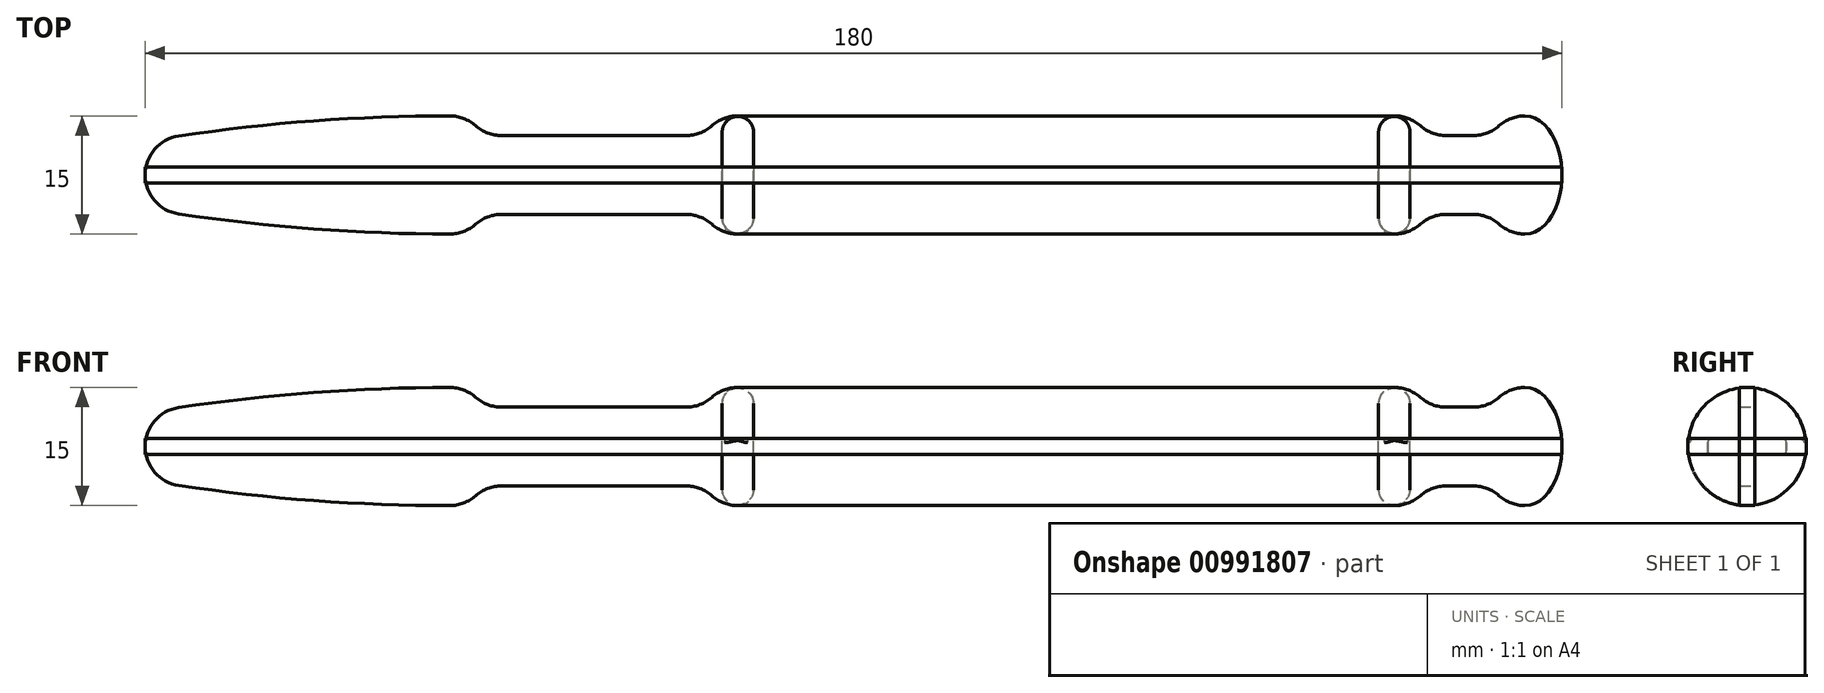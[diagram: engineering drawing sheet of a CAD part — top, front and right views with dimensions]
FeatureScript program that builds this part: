
annotation { "Feature Type Name" : "Feature", "Feature Type Description" : "" }
export const myFeature = defineFeature(function(context is Context, id is Id, definition is map)
    precondition{}
    {
        {
            var Q0;
            Q0=qCreatedBy(makeId("Top.planeOp"),FACE);
            var sketch = newSketch(context, id + "F0", { "sketchPlane" : qUnion([Q0])});
            skLineSegment(sketch, "E0", {"start": v(-90, 0) * mm, "end": v(90, 0) * mm});
            skLineSegment(sketch, "E1.top", {"start": v(-44.7, 5) * mm, "end": v(-21.3, 5) * mm});
            skLineSegment(sketch, "E2.top", {"start": v(75.3, 5) * mm, "end": v(78.7, 5) * mm});
            skLineSegment(sketch, "E3.trimOffspring", {"start": v(-14.7, 7.5) * mm, "end": v(68.7, 7.5) * mm});
            skArc(sketch, "E4.filletArc", {"start": v(72, 6.25) * mm, "mid": v(70.46, 7.18) * mm, "end": v(68.7, 7.5) * mm});
            skArc(sketch, "E5.filletArc", {"start": v(72, 6.25) * mm, "mid": v(73.54, 5.32) * mm, "end": v(75.3, 5) * mm});
            skPoint(sketch, "E6", {"position": v(77, 5) * mm});
            skArc(sketch, "E7.filletArc", {"start": v(-14.7, 7.5) * mm, "mid": v(-16.46, 7.18) * mm, "end": v(-18, 6.25) * mm});
            skArc(sketch, "E8.filletArc", {"start": v(-48, 6.25) * mm, "mid": v(-46.46, 5.32) * mm, "end": v(-44.7, 5) * mm});
            skArc(sketch, "E9.filletArc", {"start": v(-21.3, 5) * mm, "mid": v(-19.54, 5.32) * mm, "end": v(-18, 6.25) * mm});
            skArc(sketch, "E10.filletArc", {"start": v(-48, 6.25) * mm, "mid": v(-49.54, 7.18) * mm, "end": v(-51.3, 7.5) * mm});
            skArc(sketch, "E11.filletArc", {"start": v(-51.3, 7.5) * mm, "mid": v(-68.57, 6.86) * mm, "end": v(-85.74, 4.95) * mm});
            skPoint(sketch, "E12", {"position": v(-33, 5) * mm});
            skLineSegment(sketch, "E13", {"start": v(68.7, 7.5) * mm, "end": v(85.3, 7.5) * mm, "construction": true});
            skEllipticalArc(sketch, "E14", {});
            skLineSegment(sketch, "E15", {"start": v(85.3, 0) * mm, "end": v(85.3, 7.5) * mm, "construction": true});
            skArc(sketch, "E16", {"start": v(78.7, 5) * mm, "mid": v(80.46, 5.32) * mm, "end": v(82, 6.25) * mm});
            skArc(sketch, "E17", {"start": v(85.3, 7.5) * mm, "mid": v(83.54, 7.18) * mm, "end": v(82, 6.25) * mm});
            skArc(sketch, "E18", {"start": v(-85.74, 4.95) * mm, "mid": v(-88.79, 3.26) * mm, "end": v(-90, 0) * mm});
            skLineSegment(sketch, "E19", {"start": v(-51.3, 7.5) * mm, "end": v(-51.3, 0) * mm, "construction": true});
            skArc(sketch, "E20", {"start": v(-12.7, 5.5) * mm, "mid": v(-14.7, 7.5) * mm, "end": v(-16.7, 5.5) * mm});
            skLineSegment(sketch, "E21", {"start": v(-16.7, 5.5) * mm, "end": v(-16.7, 0) * mm});
            skLineSegment(sketch, "E22", {"start": v(-12.7, 5.5) * mm, "end": v(-12.7, 0) * mm});
            skArc(sketch, "E23", {"start": v(70.7, 5.5) * mm, "mid": v(68.7, 7.5) * mm, "end": v(66.7, 5.5) * mm});
            skLineSegment(sketch, "E24", {"start": v(66.7, 5.5) * mm, "end": v(66.7, 0) * mm});
            skLineSegment(sketch, "E25", {"start": v(70.7, 5.5) * mm, "end": v(70.7, 0) * mm});
            const initialGuessF0  = {"E14": [0.0853074483600893, 0, 0, 1, 0.007500455359583116, 0.004692551639910688, 4.71238898038469, 0]};
            skSetInitialGuess(sketch, initialGuessF0);
            skSolve(sketch);
        }
        {
            var Q0;
            Q0=makeQuery(id+"F0.imprint","IMPRINT",FACE,{"disambiguationData":[TD([[makeQuery(id+"F0.imprint","IMPRINT",EDGE,{"derivedFrom":sQuery(id+"F0.wireOp",EDGE,"E0")}),1.0]])]});
            var Q1;
            Q1=makeQuery(id+"F0.imprint","IMPRINT",FACE,{"disambiguationData":[TD([[makeQuery(id+"F0.imprint","IMPRINT",EDGE,{"derivedFrom":sQuery(id+"F0.wireOp",EDGE,"E1.top")}),-1.0]])]});
            var Q2;
            {var subQ1=sQuery(id+"F0.wireOp",EDGE,"E3.trimOffspring");Q2=makeQuery(id+"F0.imprint","IMPRINT",FACE,{"disambiguationData":[TD([[makeQuery(id+"F0.imprint","IMPRINT",EDGE,{"derivedFrom":subQ1}),-1.0]])]});}
            var Q3;
            Q3=makeQuery(id+"F0.imprint","IMPRINT",FACE,{"disambiguationData":[TD([[makeQuery(id+"F0.imprint","IMPRINT",EDGE,{"derivedFrom":sQuery(id+"F0.wireOp",EDGE,"E2.top")}),-1.0]])]});
            extrude(context, id + "F1", {"entities" : qUnion([Q0, Q1, Q2, Q3]), "endBound" : BoundingType.SYMMETRIC, "depth" : 2 * mm, "offsetDistance" : 25 * mm});
        }
        {
            var Q0;
            Q0=makeQuery(id+"F1.opExtrude","SWEPT_BODY",BODY,{"disambiguationData":[OSD([sQuery(id+"F0.wireOp",EDGE,"E0"),sQuery(id+"F0.wireOp",EDGE,"E1.top"),sQuery(id+"F0.wireOp",EDGE,"E2.top"),sQuery(id+"F0.wireOp",EDGE,"E3.trimOffspring"),sQuery(id+"F0.wireOp",EDGE,"E4.filletArc"),sQuery(id+"F0.wireOp",EDGE,"E5.filletArc"),sQuery(id+"F0.wireOp",EDGE,"E7.filletArc"),sQuery(id+"F0.wireOp",EDGE,"E8.filletArc"),sQuery(id+"F0.wireOp",EDGE,"E9.filletArc"),sQuery(id+"F0.wireOp",EDGE,"E10.filletArc"),sQuery(id+"F0.wireOp",EDGE,"E11.filletArc"),sQuery(id+"F0.wireOp",EDGE,"E14"),sQuery(id+"F0.wireOp",EDGE,"E16"),sQuery(id+"F0.wireOp",EDGE,"E17"),sQuery(id+"F0.wireOp",EDGE,"E18")])]});
            var Q1;
            Q1=makeQuery(id+"F1.opExtrude","SWEPT_FACE",FACE,{"disambiguationData":[OSD([sQuery(id+"F0.wireOp",EDGE,"E0")])]});
            mirror(context, id + "F2", {"operationType" : NewBodyOperationType.ADD, "entities" : qUnion([Q0]), "mirrorPlane" : qUnion([Q1])});
        }
        {
            var Q0;
            {var subQ2=sQuery(id+"F0.wireOp",EDGE,"E21");Q0=makeQuery(id+"F0.imprint","IMPRINT",FACE,{"disambiguationData":[TD([[makeQuery(id+"F0.imprint","IMPRINT",EDGE,{"derivedFrom":subQ2}),1.0]])]});}
            var Q1;
            {var subQ0=sQuery(id+"F0.wireOp",EDGE,"E24");Q1=makeQuery(id+"F0.imprint","IMPRINT",FACE,{"disambiguationData":[TD([[makeQuery(id+"F0.imprint","IMPRINT",EDGE,{"derivedFrom":subQ0}),1.0]])]});}
            var Q2;
            Q2=sQuery(id+"F0.wireOp",EDGE,"E0");
            var Q3;
            Q3=sQuery(id+"F0.wireOp",EDGE,"E0");
            revolve(context, id + "F3", {"operationType" : NewBodyOperationType.ADD, "surfaceOperationType" : NewSurfaceOperationType.NEW, "entities" : qUnion([Q0, Q1]), "surfaceEntities" : qUnion([Q2]), "axis" : qUnion([Q3]), "revolveType" : RevolveType.ONE_DIRECTION, "angle" : 180 * degree});
        }
        {
            var Q0;
            Q0=makeQuery(id+"F1.opExtrude","SWEPT_BODY",BODY,{"disambiguationData":[OSD([sQuery(id+"F0.wireOp",EDGE,"E0"),sQuery(id+"F0.wireOp",EDGE,"E1.top"),sQuery(id+"F0.wireOp",EDGE,"E2.top"),sQuery(id+"F0.wireOp",EDGE,"E3.trimOffspring"),sQuery(id+"F0.wireOp",EDGE,"E4.filletArc"),sQuery(id+"F0.wireOp",EDGE,"E5.filletArc"),sQuery(id+"F0.wireOp",EDGE,"E7.filletArc"),sQuery(id+"F0.wireOp",EDGE,"E8.filletArc"),sQuery(id+"F0.wireOp",EDGE,"E9.filletArc"),sQuery(id+"F0.wireOp",EDGE,"E10.filletArc"),sQuery(id+"F0.wireOp",EDGE,"E11.filletArc"),sQuery(id+"F0.wireOp",EDGE,"E14"),sQuery(id+"F0.wireOp",EDGE,"E16"),sQuery(id+"F0.wireOp",EDGE,"E17"),sQuery(id+"F0.wireOp",EDGE,"E18")])]});
            var Q1;
            Q1=sQuery(id+"F0.wireOp",EDGE,"E0");
            circularPattern(context, id + "F4", {"entities" : qUnion([Q0]), "axis" : qUnion([Q1]), "angle" : 180 * degree, "instanceCount" : 3, "equalSpace" : true});
        }
        {
            var Q0;
            Q0=makeQuery(id+"F2.opPattern","COPY",EDGE,{"derivedFrom":makeQuery(id+"F1.opExtrude","CAP_EDGE",EDGE,{"disambiguationData":[OSD([sQuery(id+"F0.wireOp",EDGE,"E9.filletArc")])],"isStart":false}),"instanceName":"1"});
            var Q1;
            Q1=makeQuery(id+"F2.opPattern","COPY",EDGE,{"derivedFrom":makeQuery(id+"F1.opExtrude","CAP_EDGE",EDGE,{"disambiguationData":[OSD([sQuery(id+"F0.wireOp",EDGE,"E9.filletArc")])],"isStart":true}),"instanceName":"1"});
            fillet(context, id + "F5", {"entities" : qUnion([Q0, Q1]), "radius" : 0.5 * mm, "tangentPropagation" : true, "allowEdgeOverflow" : false});
        }
    });
